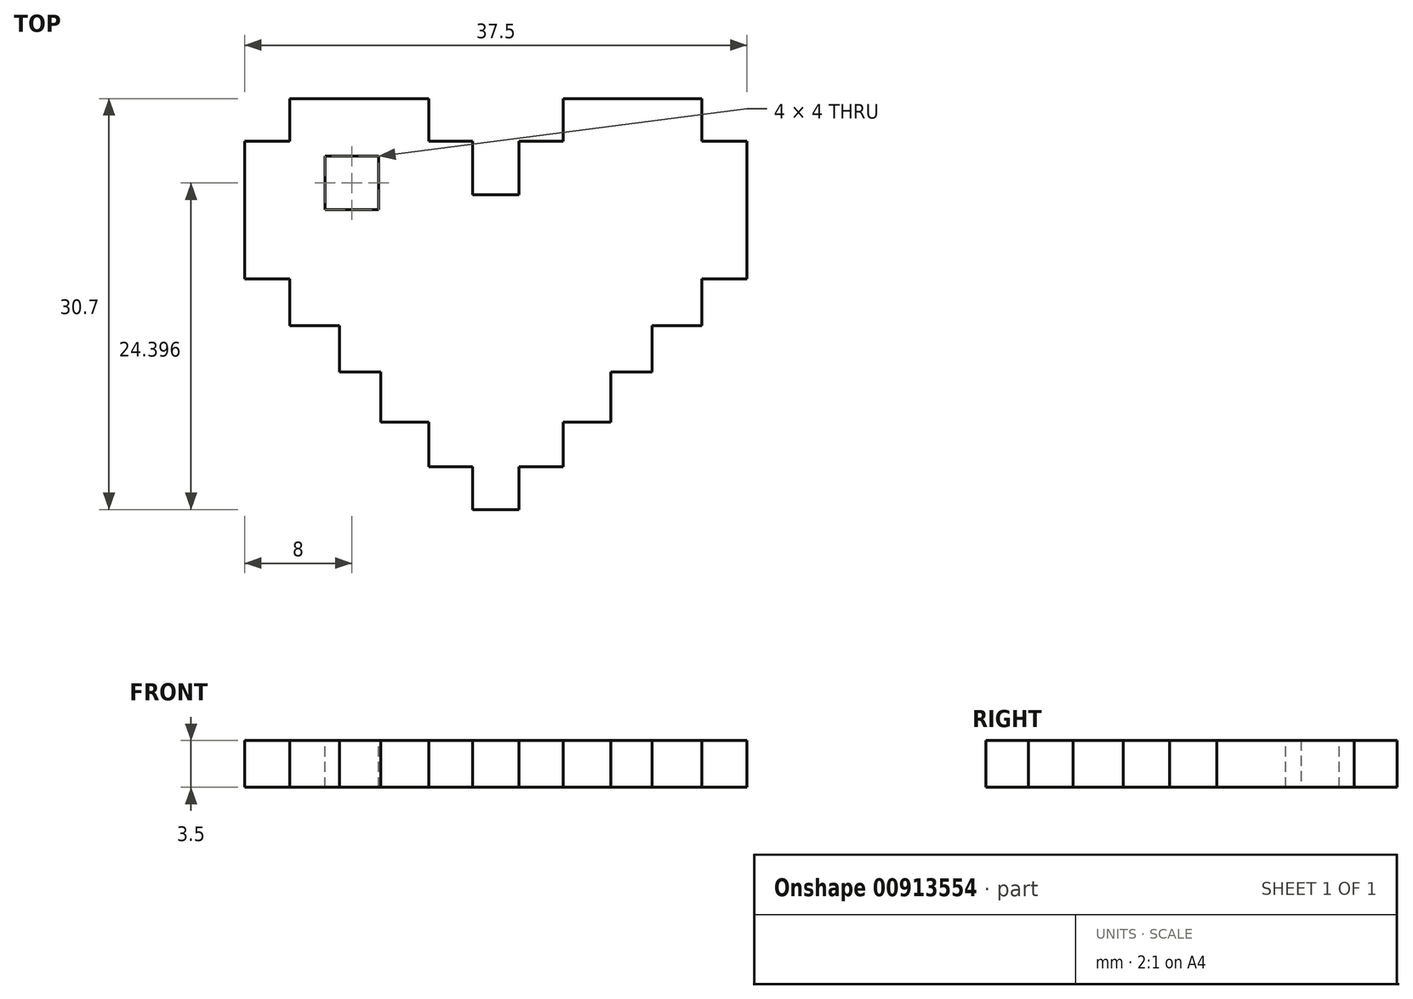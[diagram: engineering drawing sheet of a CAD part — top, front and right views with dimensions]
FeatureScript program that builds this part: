
annotation { "Feature Type Name" : "Feature", "Feature Type Description" : "" }
export const myFeature = defineFeature(function(context is Context, id is Id, definition is map)
    precondition{}
    {
        {
            var Q0;
            Q0=qCreatedBy(makeId("Top.planeOp"),FACE);
            var sketch = newSketch(context, id + "F0", { "sketchPlane" : qUnion([Q0])});
            skLineSegment(sketch, "E0", {"start": v(-18.75, 0) * mm, "end": v(18.75, 0) * mm, "construction": true});
            skLineSegment(sketch, "E1", {"start": v(0, 0) * mm, "end": v(0, 55.42) * mm, "construction": true});
            skSolve(sketch);
        }
        {
            var Q0;
            Q0=qCreatedBy(makeId("Top.planeOp"),FACE);
            var sketch = newSketch(context, id + "F1", { "sketchPlane" : qUnion([Q0])});
            skLineSegment(sketch, "E2", {"start": v(-18.75, 0) * mm, "end": v(-18.75, 4) * mm});
            skLineSegment(sketch, "E3", {"start": v(-18.75, 4) * mm, "end": v(-15.4, 4) * mm});
            skLineSegment(sketch, "E4", {"start": v(-15.4, 4) * mm, "end": v(-15.4, 7.18) * mm});
            skLineSegment(sketch, "E5", {"start": v(-15.4, 7.18) * mm, "end": v(-5.02, 7.18) * mm});
            skLineSegment(sketch, "E6", {"start": v(-5.02, 7.18) * mm, "end": v(-5.02, 4) * mm});
            skLineSegment(sketch, "E7", {"start": v(-5.02, 4) * mm, "end": v(-1.72, 4) * mm});
            skLineSegment(sketch, "E8", {"start": v(-1.72, 4) * mm, "end": v(-1.72, 0) * mm});
            skLineSegment(sketch, "E9", {"start": v(-1.72, 0) * mm, "end": v(0, 0) * mm});
            skLineSegment(sketch, "E10", {"start": v(-18.75, 0) * mm, "end": v(-18.75, -6.28) * mm});
            skLineSegment(sketch, "E11", {"start": v(-18.75, -6.28) * mm, "end": v(-15.4, -6.28) * mm});
            skLineSegment(sketch, "E12", {"start": v(-15.4, -6.28) * mm, "end": v(-15.4, -9.8) * mm});
            skLineSegment(sketch, "E13", {"start": v(-15.4, -9.8) * mm, "end": v(-11.66, -9.8) * mm});
            skLineSegment(sketch, "E14", {"start": v(-11.66, -9.8) * mm, "end": v(-11.66, -13.25) * mm});
            skLineSegment(sketch, "E15", {"start": v(-11.66, -13.25) * mm, "end": v(-8.59, -13.25) * mm});
            skLineSegment(sketch, "E16", {"start": v(-8.59, -13.25) * mm, "end": v(-8.59, -16.99) * mm});
            skLineSegment(sketch, "E17", {"start": v(-8.59, -16.99) * mm, "end": v(-5.02, -16.99) * mm});
            skLineSegment(sketch, "E18", {"start": v(-5.02, -16.99) * mm, "end": v(-5.02, -20.34) * mm});
            skLineSegment(sketch, "E19", {"start": v(-5.02, -20.34) * mm, "end": v(-1.72, -20.34) * mm});
            skLineSegment(sketch, "E20", {"start": v(-1.72, -20.34) * mm, "end": v(-1.72, -23.52) * mm});
            skLineSegment(sketch, "E21", {"start": v(-1.72, -23.52) * mm, "end": v(0, -23.52) * mm});
            skLineSegment(sketch, "E22.MirrorCS", {"start": v(1.72, 0) * mm, "end": v(0, 0) * mm});
            skLineSegment(sketch, "E23.MirrorCS", {"start": v(1.72, 4) * mm, "end": v(1.72, 0) * mm});
            skLineSegment(sketch, "E24.MirrorCS", {"start": v(5.02, 4) * mm, "end": v(1.72, 4) * mm});
            skLineSegment(sketch, "E25.MirrorCS", {"start": v(5.02, 7.18) * mm, "end": v(5.02, 4) * mm});
            skLineSegment(sketch, "E26.MirrorCS", {"start": v(15.4, -9.8) * mm, "end": v(11.66, -9.8) * mm});
            skLineSegment(sketch, "E27.MirrorCS", {"start": v(18.75, 0) * mm, "end": v(18.75, 4) * mm});
            skLineSegment(sketch, "E28.MirrorCS", {"start": v(8.59, -16.99) * mm, "end": v(5.02, -16.99) * mm});
            skLineSegment(sketch, "E29.MirrorCS", {"start": v(11.66, -13.25) * mm, "end": v(8.59, -13.25) * mm});
            skLineSegment(sketch, "E30.MirrorCS", {"start": v(11.66, -9.8) * mm, "end": v(11.66, -13.25) * mm});
            skLineSegment(sketch, "E31.MirrorCS", {"start": v(15.4, -6.28) * mm, "end": v(15.4, -9.8) * mm});
            skLineSegment(sketch, "E32.MirrorCS", {"start": v(18.75, 0) * mm, "end": v(18.75, -6.28) * mm});
            skLineSegment(sketch, "E33.MirrorCS", {"start": v(15.4, 4) * mm, "end": v(15.4, 7.18) * mm});
            skLineSegment(sketch, "E34.MirrorCS", {"start": v(15.4, 7.18) * mm, "end": v(5.02, 7.18) * mm});
            skLineSegment(sketch, "E35.MirrorCS", {"start": v(18.75, 4) * mm, "end": v(15.4, 4) * mm});
            skLineSegment(sketch, "E36.MirrorCS", {"start": v(18.75, -6.28) * mm, "end": v(15.4, -6.28) * mm});
            skLineSegment(sketch, "E37.MirrorCS", {"start": v(8.59, -13.25) * mm, "end": v(8.59, -16.99) * mm});
            skLineSegment(sketch, "E38.MirrorCS", {"start": v(5.02, -20.34) * mm, "end": v(1.72, -20.34) * mm});
            skLineSegment(sketch, "E39.MirrorCS", {"start": v(1.72, -23.52) * mm, "end": v(0, -23.52) * mm});
            skLineSegment(sketch, "E40.MirrorCS", {"start": v(1.72, -20.34) * mm, "end": v(1.72, -23.52) * mm});
            skLineSegment(sketch, "E41.MirrorCS", {"start": v(5.02, -16.99) * mm, "end": v(5.02, -20.34) * mm});
            skSolve(sketch);
        }
        {
            var Q0;
            Q0 = qSketchRegion(id + "F1", true);
            extrude(context, id + "F2", {"entities" : qUnion([Q0]), "depth" : 3.5 * mm, "offsetDistance" : 25 * mm});
        }
        {
            var Q0;
            Q0=makeQuery(id+"F2.opExtrude","CAP_FACE",FACE,{"disambiguationData":[OSD([sQuery(id+"F1.wireOp",EDGE,"E2"),sQuery(id+"F1.wireOp",EDGE,"E3"),sQuery(id+"F1.wireOp",EDGE,"E4"),sQuery(id+"F1.wireOp",EDGE,"E5"),sQuery(id+"F1.wireOp",EDGE,"E6"),sQuery(id+"F1.wireOp",EDGE,"E7"),sQuery(id+"F1.wireOp",EDGE,"E8"),sQuery(id+"F1.wireOp",EDGE,"E9"),sQuery(id+"F1.wireOp",EDGE,"E10"),sQuery(id+"F1.wireOp",EDGE,"E11"),sQuery(id+"F1.wireOp",EDGE,"E12"),sQuery(id+"F1.wireOp",EDGE,"E13"),sQuery(id+"F1.wireOp",EDGE,"E14"),sQuery(id+"F1.wireOp",EDGE,"E15"),sQuery(id+"F1.wireOp",EDGE,"E16"),sQuery(id+"F1.wireOp",EDGE,"E17"),sQuery(id+"F1.wireOp",EDGE,"E18"),sQuery(id+"F1.wireOp",EDGE,"E19"),sQuery(id+"F1.wireOp",EDGE,"E20"),sQuery(id+"F1.wireOp",EDGE,"E21"),sQuery(id+"F1.wireOp",EDGE,"E22.MirrorCS"),sQuery(id+"F1.wireOp",EDGE,"E23.MirrorCS"),sQuery(id+"F1.wireOp",EDGE,"E24.MirrorCS"),sQuery(id+"F1.wireOp",EDGE,"E25.MirrorCS"),sQuery(id+"F1.wireOp",EDGE,"E26.MirrorCS"),sQuery(id+"F1.wireOp",EDGE,"E28.MirrorCS"),sQuery(id+"F1.wireOp",EDGE,"E29.MirrorCS"),sQuery(id+"F1.wireOp",EDGE,"E30.MirrorCS"),sQuery(id+"F1.wireOp",EDGE,"E31.MirrorCS"),sQuery(id+"F1.wireOp",EDGE,"E33.MirrorCS"),sQuery(id+"F1.wireOp",EDGE,"E34.MirrorCS"),sQuery(id+"F1.wireOp",EDGE,"E35.MirrorCS"),sQuery(id+"F1.wireOp",EDGE,"E36.MirrorCS"),sQuery(id+"F1.wireOp",EDGE,"E37.MirrorCS"),sQuery(id+"F1.wireOp",EDGE,"E38.MirrorCS"),sQuery(id+"F1.wireOp",EDGE,"E39.MirrorCS"),sQuery(id+"F1.wireOp",EDGE,"E40.MirrorCS"),sQuery(id+"F1.wireOp",EDGE,"E41.MirrorCS"),sQuery(id+"F1.wireOp",EDGE,"E32.MirrorCS"),sQuery(id+"F1.wireOp",EDGE,"E27.MirrorCS")])],"isStart":false});
            var sketch = newSketch(context, id + "F3", { "sketchPlane" : qUnion([Q0])});
            skLineSegment(sketch, "E42.bottom", {"start": v(-12.75, 2.88) * mm, "end": v(-8.75, 2.88) * mm});
            skLineSegment(sketch, "E42.top", {"start": v(-12.75, -1.12) * mm, "end": v(-8.75, -1.12) * mm});
            skLineSegment(sketch, "E42.left", {"start": v(-12.75, 2.88) * mm, "end": v(-12.75, -1.12) * mm});
            skLineSegment(sketch, "E42.right", {"start": v(-8.75, 2.88) * mm, "end": v(-8.75, -1.12) * mm});
            skSolve(sketch);
        }
        {
            var Q0;
            Q0=makeQuery(id+"F3.imprint","IMPRINT",FACE,{"disambiguationData":[TD([[makeQuery(id+"F3.imprint","IMPRINT",EDGE,{"derivedFrom":sQuery(id+"F3.wireOp",EDGE,"E42.bottom")}),-1.0]])]});
            extrude(context, id + "F4", {"entities" : qUnion([Q0]), "operationType" : NewBodyOperationType.REMOVE, "endBound" : BoundingType.THROUGH_ALL, "oppositeDirection" : true, "depth" : 25 * mm, "offsetDistance" : 25 * mm});
        }
    });
